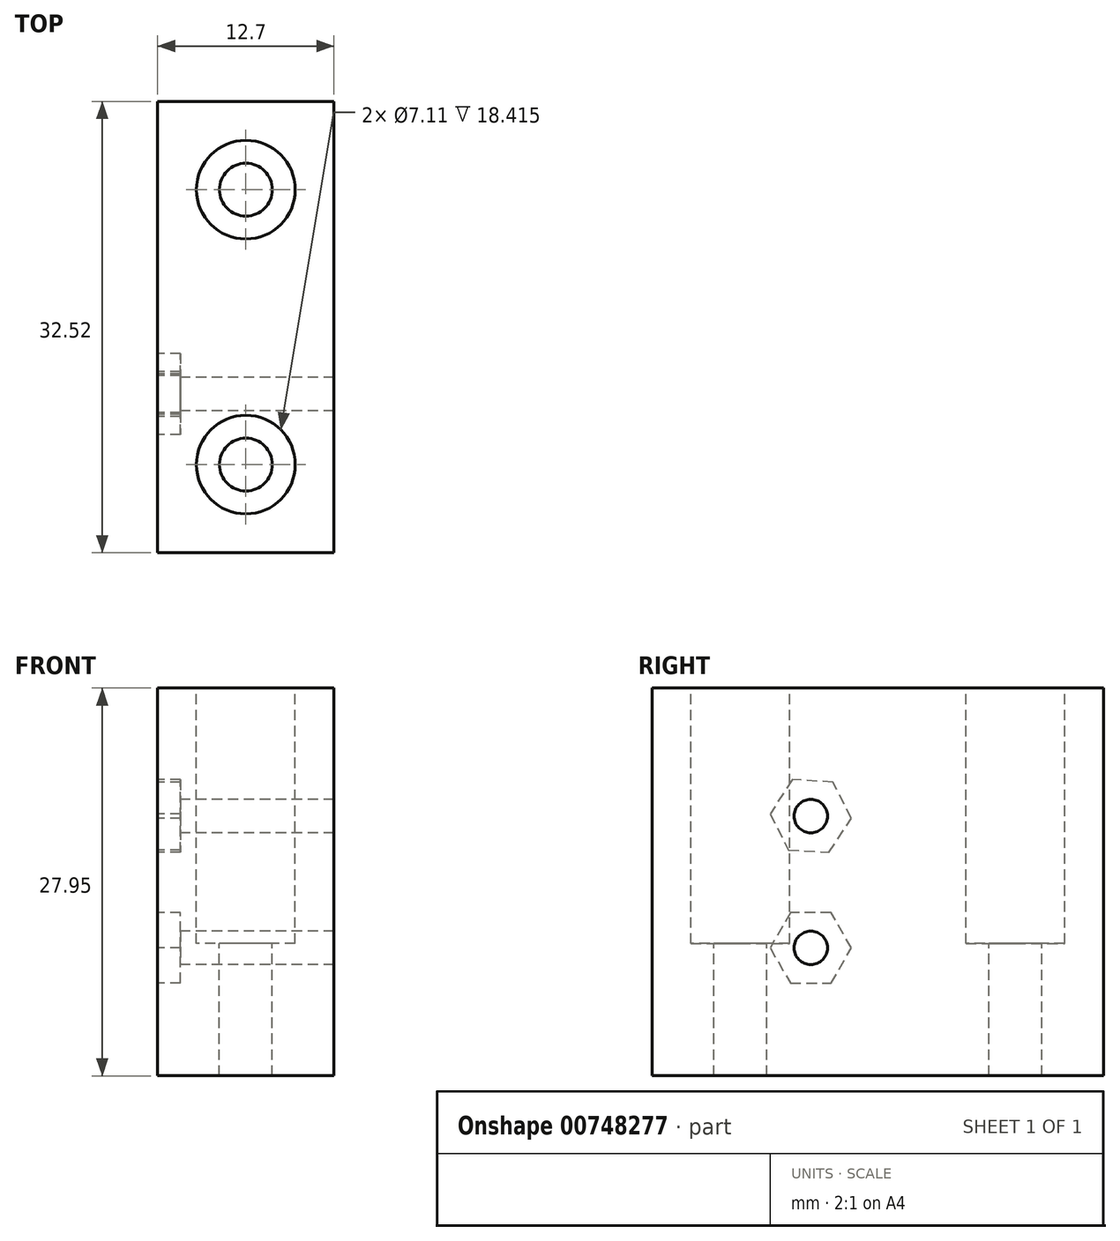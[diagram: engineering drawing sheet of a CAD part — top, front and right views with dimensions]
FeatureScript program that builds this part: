
annotation { "Feature Type Name" : "Feature", "Feature Type Description" : "" }
export const myFeature = defineFeature(function(context is Context, id is Id, definition is map)
    precondition{}
    {
        {
            var Q0;
            Q0=qCreatedBy(makeId("Right.planeOp"),FACE);
            var sketch = newSketch(context, id + "F0", { "sketchPlane" : qUnion([Q0])});
            skLineSegment(sketch, "E0.bottom", {"start": v(9.9, 9.53) * mm, "end": v(-9.9, 9.53) * mm, "construction": true});
            skLineSegment(sketch, "E0.top", {"start": v(9.9, -9.53) * mm, "end": v(-9.9, -9.53) * mm, "construction": true});
            skLineSegment(sketch, "E0.left", {"start": v(9.9, 9.53) * mm, "end": v(9.9, -9.53) * mm, "construction": true});
            skLineSegment(sketch, "E0.right", {"start": v(-9.9, 9.53) * mm, "end": v(-9.9, -9.52) * mm, "construction": true});
            skPoint(sketch, "E0.middle", {"position": v(0, 0) * mm});
            skLineSegment(sketch, "E1", {"start": v(16.26, -9.52) * mm, "end": v(16.26, 18.42) * mm});
            skLineSegment(sketch, "E2", {"start": v(-16.26, -9.53) * mm, "end": v(-16.26, 18.42) * mm});
            skLineSegment(sketch, "E3", {"start": v(-16.26, 18.42) * mm, "end": v(16.26, 18.42) * mm});
            skLineSegment(sketch, "E4", {"start": v(16.26, -9.52) * mm, "end": v(-16.26, -9.52) * mm});
            skSolve(sketch);
        }
        {
            var Q0;
            Q0 = qSketchRegion(id + "F0", true);
            extrude(context, id + "F1", {"entities" : qUnion([Q0]), "depth" : 12.7 * mm, "offsetDistance" : 25.4 * mm});
        }
        {
            var Q0;
            Q0=makeQuery(id+"F1.opExtrude","CAP_FACE",FACE,{"disambiguationData":[OSD([sQuery(id+"F0.wireOp",EDGE,"E1"),sQuery(id+"F0.wireOp",EDGE,"E2"),sQuery(id+"F0.wireOp",EDGE,"E3"),sQuery(id+"F0.wireOp",EDGE,"E4")])],"isStart":true});
            var sketch = newSketch(context, id + "F2", { "sketchPlane" : qUnion([Q0])});
            skPoint(sketch, "E5.middle", {"position": v(0, 0) * mm});
            skCircle(sketch, "E6", {"center": v(4.83, -0.3) * mm, "radius": 1.2 * mm});
            skCircle(sketch, "E7", {"center": v(4.83, 9.2) * mm, "radius": 1.2 * mm});
            skLineSegment(sketch, "E8", {"start": v(16.26, 4.45) * mm, "end": v(-16.26, 4.45) * mm, "construction": true});
            skLineSegment(sketch, "E9.0", {"start": v(16.26, 9.2) * mm, "end": v(-16.26, 9.2) * mm, "construction": true});
            skLineSegment(sketch, "E10.0", {"start": v(16.26, -0.3) * mm, "end": v(-16.26, -0.3) * mm, "construction": true});
            skLineSegment(sketch, "E11", {"start": v(4.83, 18.42) * mm, "end": v(4.83, -9.52) * mm, "construction": true});
            skSolve(sketch);
        }
        {
            var Q0;
            Q0 = qSketchRegion(id + "F2", true);
            extrude(context, id + "F3", {"entities" : qUnion([Q0]), "operationType" : NewBodyOperationType.REMOVE, "endBound" : BoundingType.THROUGH_ALL, "oppositeDirection" : true, "depth" : 25.4 * mm, "offsetDistance" : 25.4 * mm});
        }
        {
            var Q0;
            Q0=makeQuery(id+"F1.opExtrude","CAP_FACE",FACE,{"disambiguationData":[OSD([sQuery(id+"F0.wireOp",EDGE,"E1"),sQuery(id+"F0.wireOp",EDGE,"E2"),sQuery(id+"F0.wireOp",EDGE,"E3"),sQuery(id+"F0.wireOp",EDGE,"E4")])],"isStart":true});
            var sketch = newSketch(context, id + "F4", { "sketchPlane" : qUnion([Q0])});
            skCircle(sketch, "E12.cCircle", {"center": v(4.83, 9.2) * mm, "radius": 2.54 * mm, "construction": true});
            skLineSegment(sketch, "E12.0", {"start": v(6.15, 11.81) * mm, "end": v(7.75, 9.36) * mm});
            skLineSegment(sketch, "E12.1", {"start": v(7.75, 9.36) * mm, "end": v(6.43, 6.74) * mm});
            skLineSegment(sketch, "E12.2", {"start": v(6.43, 6.74) * mm, "end": v(3.5, 6.58) * mm});
            skLineSegment(sketch, "E12.3", {"start": v(3.5, 6.58) * mm, "end": v(1.9, 9.03) * mm});
            skLineSegment(sketch, "E12.4", {"start": v(1.9, 9.03) * mm, "end": v(3.22, 11.65) * mm});
            skLineSegment(sketch, "E12.5", {"start": v(3.22, 11.65) * mm, "end": v(6.15, 11.81) * mm});
            skPoint(sketch, "E12.0.midPoint", {"position": v(6.95, 10.59) * mm});
            skCircle(sketch, "E13.cCircle", {"center": v(4.83, -0.3) * mm, "radius": 2.54 * mm, "construction": true});
            skLineSegment(sketch, "E13.0", {"start": v(3.36, 2.24) * mm, "end": v(6.3, 2.24) * mm});
            skLineSegment(sketch, "E13.1", {"start": v(6.3, 2.24) * mm, "end": v(7.76, -0.3) * mm});
            skLineSegment(sketch, "E13.2", {"start": v(7.76, -0.3) * mm, "end": v(6.3, -2.84) * mm});
            skLineSegment(sketch, "E13.3", {"start": v(6.3, -2.84) * mm, "end": v(3.36, -2.84) * mm});
            skLineSegment(sketch, "E13.4", {"start": v(3.36, -2.84) * mm, "end": v(1.9, -0.3) * mm});
            skLineSegment(sketch, "E13.5", {"start": v(1.9, -0.3) * mm, "end": v(3.36, 2.24) * mm});
            skPoint(sketch, "E13.0.midPoint", {"position": v(4.83, 2.24) * mm});
            skSolve(sketch);
        }
        {
            var Q0;
            Q0 = qSketchRegion(id + "F4", true);
            extrude(context, id + "F5", {"entities" : qUnion([Q0]), "operationType" : NewBodyOperationType.REMOVE, "oppositeDirection" : true, "depth" : 1.65 * mm, "offsetDistance" : 25.4 * mm});
        }
        {
            var Q0;
            Q0=makeQuery(id+"F1.opExtrude","SWEPT_FACE",FACE,{"disambiguationData":[OSD([sQuery(id+"F0.wireOp",EDGE,"E3")])]});
            var sketch = newSketch(context, id + "F6", { "sketchPlane" : qUnion([Q0])});
            skLineSegment(sketch, "E14", {"start": v(6.35, 16.26) * mm, "end": v(6.35, -16.26) * mm, "construction": true});
            skLineSegment(sketch, "E15", {"start": v(0, 9.9) * mm, "end": v(12.7, 9.9) * mm, "construction": true});
            skLineSegment(sketch, "E16", {"start": v(0, -9.9) * mm, "end": v(12.7, -9.9) * mm, "construction": true});
            skCircle(sketch, "E17", {"center": v(6.35, -9.9) * mm, "radius": 1.9 * mm});
            skCircle(sketch, "E18", {"center": v(6.35, 9.9) * mm, "radius": 1.9 * mm});
            skSolve(sketch);
        }
        {
            var Q0;
            Q0 = qSketchRegion(id + "F6", true);
            extrude(context, id + "F7", {"entities" : qUnion([Q0]), "operationType" : NewBodyOperationType.REMOVE, "endBound" : BoundingType.THROUGH_ALL, "oppositeDirection" : true, "depth" : 25.4 * mm, "offsetDistance" : 25.4 * mm});
        }
        {
            var Q0;
            Q0=makeQuery(id+"F1.opExtrude","SWEPT_FACE",FACE,{"disambiguationData":[OSD([sQuery(id+"F0.wireOp",EDGE,"E3")])]});
            var sketch = newSketch(context, id + "F8", { "sketchPlane" : qUnion([Q0])});
            skCircle(sketch, "E19", {"center": v(6.35, 9.9) * mm, "radius": 3.56 * mm});
            skCircle(sketch, "E20", {"center": v(6.35, -9.9) * mm, "radius": 3.56 * mm});
            skSolve(sketch);
        }
        {
            var Q0;
            Q0 = qSketchRegion(id + "F8", true);
            extrude(context, id + "F9", {"entities" : qUnion([Q0]), "operationType" : NewBodyOperationType.REMOVE, "oppositeDirection" : true, "depth" : 18.42 * mm, "offsetDistance" : 25.4 * mm});
        }
    });
